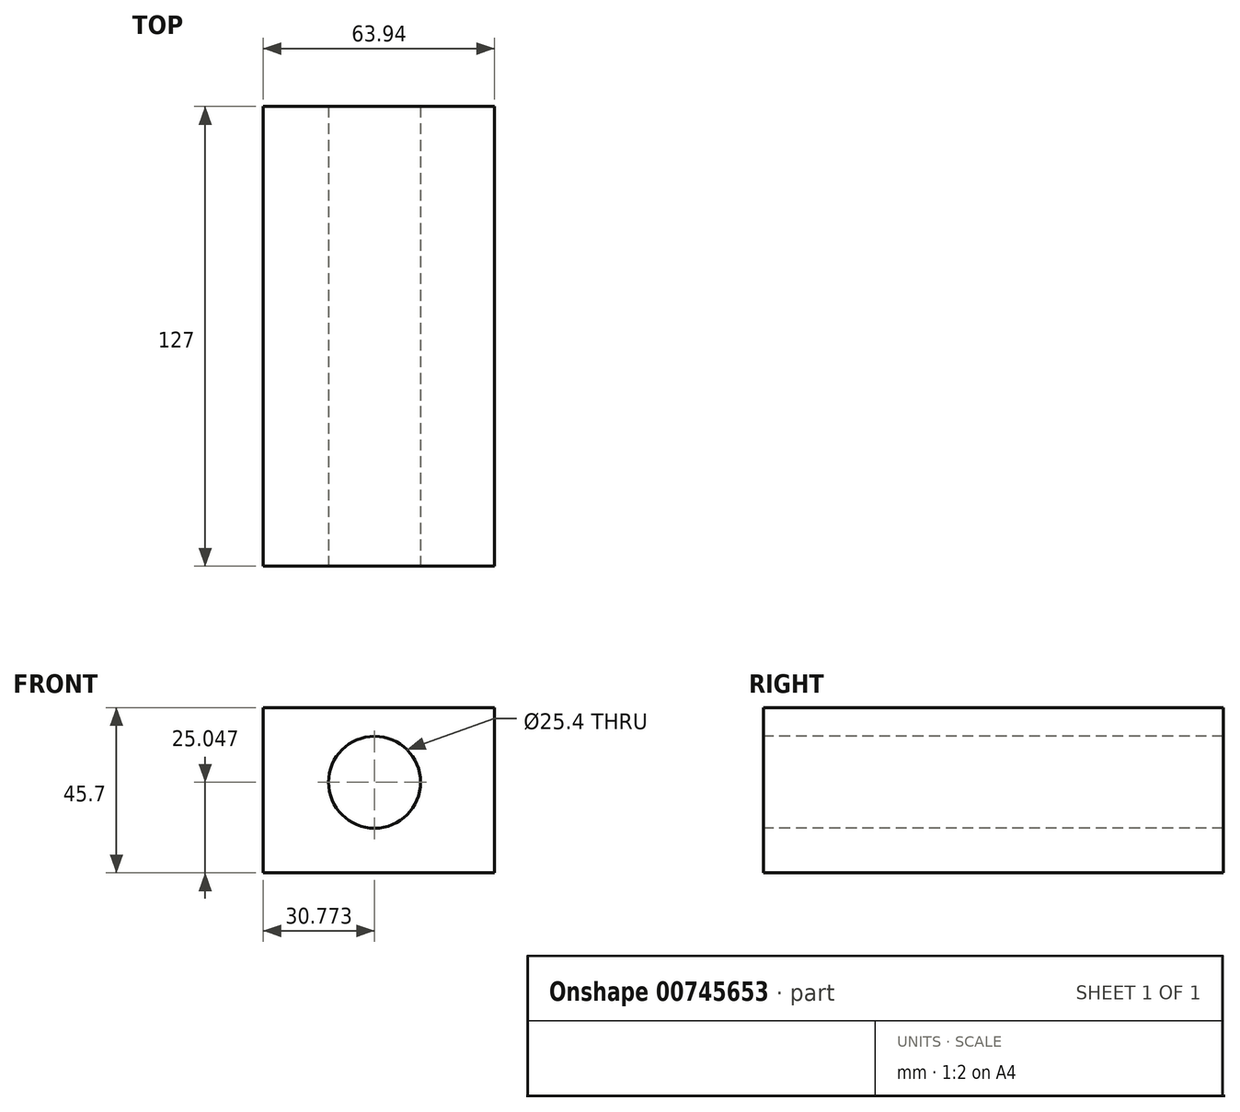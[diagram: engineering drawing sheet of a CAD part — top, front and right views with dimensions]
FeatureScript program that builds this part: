
annotation { "Feature Type Name" : "Feature", "Feature Type Description" : "" }
export const myFeature = defineFeature(function(context is Context, id is Id, definition is map)
    precondition{}
    {
        {
            var Q0;
            Q0=qCreatedBy(makeId("Front.planeOp"),FACE);
            var sketch = newSketch(context, id + "F0", { "sketchPlane" : qUnion([Q0])});
            skLineSegment(sketch, "E0", {"start": v(0, 0) * mm, "end": v(-63.94, 0) * mm});
            skLineSegment(sketch, "E1", {"start": v(-63.94, 0) * mm, "end": v(-63.94, 45.7) * mm});
            skLineSegment(sketch, "E2", {"start": v(-63.94, 45.7) * mm, "end": v(0, 45.7) * mm});
            skLineSegment(sketch, "E3", {"start": v(0, 45.7) * mm, "end": v(0, 0) * mm});
            skSolve(sketch);
        }
        {
            var Q0;
            Q0=makeQuery(id+"F0.imprint","IMPRINT",FACE,{"disambiguationData":[TD([[makeQuery(id+"F0.imprint","IMPRINT",EDGE,{"derivedFrom":sQuery(id+"F0.wireOp",EDGE,"E0")}),-1.0]])]});
            extrude(context, id + "F1", {"entities" : qUnion([Q0]), "depth" : 127 * mm, "offsetDistance" : 25.4 * mm});
        }
        {
            var Q0;
            Q0=makeQuery(id+"F1.opExtrude","CAP_FACE",FACE,{"disambiguationData":[OSD([sQuery(id+"F0.wireOp",EDGE,"E0"),sQuery(id+"F0.wireOp",EDGE,"E1"),sQuery(id+"F0.wireOp",EDGE,"E2"),sQuery(id+"F0.wireOp",EDGE,"E3")])],"isStart":false});
            var sketch = newSketch(context, id + "F2", { "sketchPlane" : qUnion([Q0])});
            skPoint(sketch, "E4", {"position": v(-33.17, 25.05) * mm});
            skSolve(sketch);
        }
        {
            var Q0;
            Q0=sQuery(id+"F2.wireOp",VERTEX,"E4");
            var Q1;
            Q1=makeQuery(id+"F1.opExtrude","SWEPT_BODY",BODY,{"disambiguationData":[OSD([sQuery(id+"F0.wireOp",EDGE,"E0"),sQuery(id+"F0.wireOp",EDGE,"E1"),sQuery(id+"F0.wireOp",EDGE,"E2"),sQuery(id+"F0.wireOp",EDGE,"E3")])]});
            hole(context, id + "F3", {"style" : HoleStyle.SIMPLE, "endStyle" : HoleEndStyle.THROUGH, "holeDiameter" : 25.4 * mm, "majorDiameter" : 6.35 * mm, "isTappedThrough" : true, "tappedDepth" : 12.7 * mm, "tapClearance" : 3, "locations" : qUnion([Q0]), "scope" : qUnion([Q1])});
        }
    });
